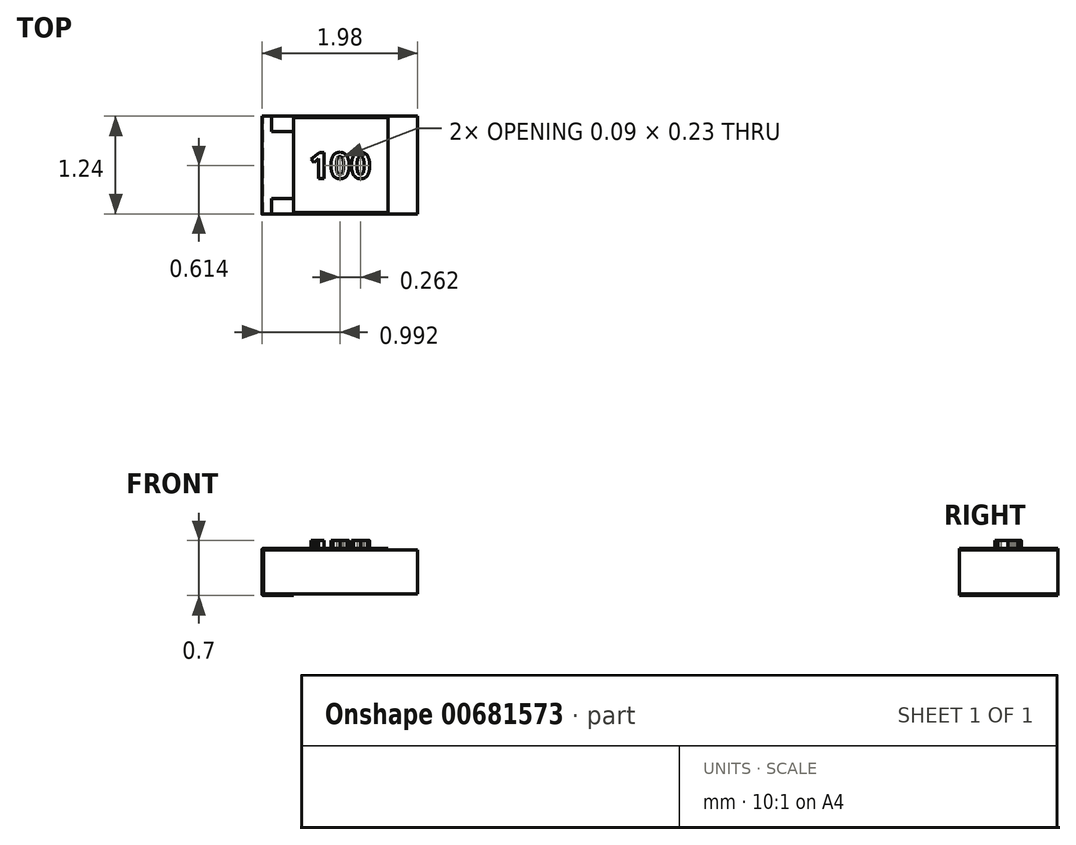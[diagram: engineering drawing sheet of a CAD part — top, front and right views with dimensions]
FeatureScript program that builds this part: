
annotation { "Feature Type Name" : "Feature", "Feature Type Description" : "" }
export const myFeature = defineFeature(function(context is Context, id is Id, definition is map)
    precondition{}
    {
        {
            assignVariable(context, id + "F0", {"name" : "size", "anyValue" : 3});
        }
        {
            assignVariable(context, id + "F1", {"name" : "width", "anyValue" : [.3, .5, .8, 1.25, 1.6, 2.5, 3.2, 2.5, 3.2][getVariable(context, 'size')]});
        }
        {
            assignVariable(context, id + "F2", {"name" : "r", "anyValue" : [0.02, 0.02, 0.02, 0.02, 0.02, 0.02, 0.02, 0.02, 0.02][getVariable(context, 'size')]});
        }
        {
            var Q0;
            Q0=qCreatedBy(makeId("Front.planeOp"),FACE);
            var sketch = newSketch(context, id + "F3", { "sketchPlane" : qUnion([Q0])});
            skLineSegment(sketch, "E0", {"start": v(-0.6, 0.6) * mm, "end": v(-0.98, 0.6) * mm});
            skLineSegment(sketch, "E1", {"start": v(-1, 0.58) * mm, "end": v(-1, 0.02) * mm});
            skLineSegment(sketch, "E2", {"start": v(-0.98, 0) * mm, "end": v(-0.6, 0) * mm});
            skLineSegment(sketch, "E3", {"start": v(-0.6, 0) * mm, "end": v(-0.6, 0.02) * mm});
            skLineSegment(sketch, "E4", {"start": v(-0.6, 0.02) * mm, "end": v(-0.98, 0.02) * mm});
            skLineSegment(sketch, "E5", {"start": v(-0.98, 0.02) * mm, "end": v(-0.98, 0.58) * mm});
            skLineSegment(sketch, "E6", {"start": v(-0.98, 0.58) * mm, "end": v(-0.6, 0.58) * mm});
            skLineSegment(sketch, "E7", {"start": v(-0.6, 0.58) * mm, "end": v(-0.6, 0.6) * mm});
            skLineSegment(sketch, "E8", {"start": v(-1, 0.3) * mm, "end": v(-0.98, 0.3) * mm, "construction": true});
            skPoint(sketch, "E9.visualSharp", {"position": v(-1, 0.6) * mm});
            skArc(sketch, "E9.filletArc", {"start": v(-0.98, 0.6) * mm, "mid": v(-1, 0.6) * mm, "end": v(-1, 0.58) * mm});
            skPoint(sketch, "E10.visualSharp", {"position": v(-1, 0) * mm});
            skArc(sketch, "E10.filletArc", {"start": v(-1, 0.02) * mm, "mid": v(-1, 0) * mm, "end": v(-0.98, 0) * mm});
            skArc(sketch, "E11.MirrorCS", {"start": v(1, 0.02) * mm, "mid": v(1, 0) * mm, "end": v(0.98, 0) * mm});
            skArc(sketch, "E12.MirrorCS", {"start": v(0.98, 0.6) * mm, "mid": v(1, 0.6) * mm, "end": v(1, 0.58) * mm});
            skLineSegment(sketch, "E13.MirrorCS", {"start": v(0.6, 0) * mm, "end": v(0.6, 0.02) * mm});
            skLineSegment(sketch, "E14.MirrorCS", {"start": v(0.6, 0.58) * mm, "end": v(0.6, 0.6) * mm});
            skLineSegment(sketch, "E15.MirrorCS", {"start": v(1, 0.3) * mm, "end": v(0.98, 0.3) * mm, "construction": true});
            skLineSegment(sketch, "E16.MirrorCS", {"start": v(1, 0.58) * mm, "end": v(1, 0.02) * mm});
            skLineSegment(sketch, "E17.MirrorCS", {"start": v(0.98, 0) * mm, "end": v(0.6, 0) * mm});
            skPoint(sketch, "E18.MirrorP", {"position": v(1, 0) * mm});
            skPoint(sketch, "E19.MirrorP", {"position": v(1, 0.6) * mm});
            skLineSegment(sketch, "E20.MirrorCS", {"start": v(0.6, 0.6) * mm, "end": v(0.98, 0.6) * mm});
            skLineSegment(sketch, "E21.MirrorCS", {"start": v(0.6, 0.02) * mm, "end": v(0.98, 0.02) * mm});
            skLineSegment(sketch, "E22.MirrorCS", {"start": v(0.98, 0.58) * mm, "end": v(0.6, 0.58) * mm});
            skLineSegment(sketch, "E23.MirrorCS", {"start": v(0.98, 0.02) * mm, "end": v(0.98, 0.58) * mm});
            skLineSegment(sketch, "E24", {"start": v(0.6, 0.58) * mm, "end": v(0.98, 0.58) * mm});
            skLineSegment(sketch, "E25", {"start": v(0.98, 0.02) * mm, "end": v(-0.98, 0.02) * mm});
            skLineSegment(sketch, "E26.bottom", {"start": v(-0.98, 0.58) * mm, "end": v(0.98, 0.58) * mm});
            skLineSegment(sketch, "E26.top", {"start": v(-0.98, 0.02) * mm, "end": v(0.98, 0.02) * mm});
            skLineSegment(sketch, "E26.left", {"start": v(-0.98, 0.58) * mm, "end": v(-0.98, 0.02) * mm});
            skLineSegment(sketch, "E26.right", {"start": v(0.98, 0.58) * mm, "end": v(0.98, 0.02) * mm});
            skLineSegment(sketch, "E27.bottom", {"start": v(-0.6, 0.6) * mm, "end": v(0.6, 0.6) * mm});
            skLineSegment(sketch, "E27.top", {"start": v(-0.6, 0.6) * mm, "end": v(0.6, 0.6) * mm});
            skLineSegment(sketch, "E27.left", {"start": v(-0.6, 0.6) * mm, "end": v(-0.6, 0.6) * mm});
            skLineSegment(sketch, "E27.right", {"start": v(0.6, 0.6) * mm, "end": v(0.6, 0.6) * mm});
            skLineSegment(sketch, "E28.bottom", {"start": v(0.6, 0.58) * mm, "end": v(-0.6, 0.58) * mm});
            skLineSegment(sketch, "E28.top", {"start": v(0.6, 0.58) * mm, "end": v(-0.6, 0.58) * mm});
            skLineSegment(sketch, "E28.left", {"start": v(0.6, 0.58) * mm, "end": v(0.6, 0.58) * mm});
            skLineSegment(sketch, "E28.right", {"start": v(-0.6, 0.58) * mm, "end": v(-0.6, 0.58) * mm});
            skSolve(sketch);
        }
        {
            var Q0;
            Q0=makeQuery(id+"F3.imprint","IMPRINT",FACE,{"disambiguationData":[TD([[makeQuery(id+"F3.imprint","IMPRINT",EDGE,{"derivedFrom":sQuery(id+"F3.wireOp",EDGE,"E0")}),1.0]])]});
            var Q1;
            Q1=makeQuery(id+"F3.imprint","IMPRINT",FACE,{"disambiguationData":[TD([[makeQuery(id+"F3.imprint","IMPRINT",EDGE,{"derivedFrom":sQuery(id+"F3.wireOp",EDGE,"E11.MirrorCS")}),-1.0]])]});
            extrude(context, id + "F4", {"entities" : qUnion([Q0, Q1]), "endBound" : BoundingType.SYMMETRIC, "depth" : (getVariable(context, 'width')) * mm, "offsetDistance" : 25 * mm});
        }
        {
            var Q0;
            Q0=makeQuery(id+"F3.imprint","IMPRINT",FACE,{"disambiguationData":[TD([[makeQuery(id+"F3.imprint","IMPRINT",EDGE,{"derivedFrom":sQuery(id+"F3.wireOp",EDGE,"E4")}),-1.0]])]});
            extrude(context, id + "F5", {"entities" : qUnion([Q0]), "endBound" : BoundingType.SYMMETRIC, "depth" : (getVariable(context, 'width')) * mm, "offsetDistance" : 25 * mm});
        }
        {
            var Q0;
            Q0=makeQuery(id+"F3.imprint","IMPRINT",FACE,{"disambiguationData":[TD([[makeQuery(id+"F3.imprint","IMPRINT",EDGE,{"derivedFrom":sQuery(id+"F3.wireOp",EDGE,"E7")}),-1.0]])]});
            extrude(context, id + "F6", {"entities" : qUnion([Q0]), "endBound" : BoundingType.SYMMETRIC, "depth" : ((getVariable(context, 'width')) - 2 * getVariable(context, 'r')) * mm, "offsetDistance" : 25 * mm});
        }
        {
            var Q0;
            Q0=makeQuery(id+"F6.opExtrude","SWEPT_FACE",FACE,{"disambiguationData":[OSD([sQuery(id+"F3.wireOp",EDGE,"E27.bottom")])]});
            var sketch = newSketch(context, id + "F7", { "sketchPlane" : qUnion([Q0])});
            skText(sketch, "E29", { "text": "100", "fontName": "OpenSans-Bold.ttf"});
            skPoint(sketch, "E30", {"position": v(0, 0) * mm});
            const initialGuessF7  = {"E29": [-0.0004, -0.00017, 1, 0, 0.00033]};
            skSetInitialGuess(sketch, initialGuessF7);
            skSolve(sketch);
        }
        {
            var Q0;
            Q0=makeQuery(id+"F7.imprint","IMPRINT",FACE,{"disambiguationData":[TD([[makeQuery(id+"F7.imprint","IMPRINT",EDGE,{"derivedFrom":sQuery(id+"F7.wireOp",EDGE,"E29.sketch_text.stroke-0")}),-1.0]])]});
            var Q1;
            Q1=makeQuery(id+"F7.imprint","IMPRINT",FACE,{"disambiguationData":[TD([[makeQuery(id+"F7.imprint","IMPRINT",EDGE,{"derivedFrom":sQuery(id+"F7.wireOp",EDGE,"E29.sketch_text.stroke-10")}),-1.0]])]});
            var Q2;
            Q2=makeQuery(id+"F7.imprint","IMPRINT",FACE,{"disambiguationData":[TD([[makeQuery(id+"F7.imprint","IMPRINT",EDGE,{"derivedFrom":sQuery(id+"F7.wireOp",EDGE,"E29.sketch_text.stroke-26")}),-1.0]])]});
            extrude(context, id + "F8", {"entities" : qUnion([Q0, Q1, Q2]), "depth" : .1 * mm, "offsetDistance" : 25 * mm});
        }
        {
            var Q0;
            Q0=makeQuery(id+"F4.opExtrude","SWEPT_FACE",FACE,{"disambiguationData":[OSD([sQuery(id+"F3.wireOp",EDGE,"E0")])]});
            var sketch = newSketch(context, id + "F9", { "sketchPlane" : qUnion([Q0])});
            skLineSegment(sketch, "E31.bottom", {"start": v(-0.6, -0.62) * mm, "end": v(-0.88, -0.62) * mm});
            skLineSegment(sketch, "E31.top", {"start": v(-0.6, -0.42) * mm, "end": v(-0.88, -0.42) * mm});
            skLineSegment(sketch, "E31.left", {"start": v(-0.6, -0.62) * mm, "end": v(-0.6, -0.42) * mm});
            skLineSegment(sketch, "E31.right", {"start": v(-0.88, -0.62) * mm, "end": v(-0.88, -0.42) * mm});
            skLineSegment(sketch, "E32.MirrorCS", {"start": v(-0.6, 0.42) * mm, "end": v(-0.88, 0.42) * mm});
            skLineSegment(sketch, "E33.MirrorCS", {"start": v(-0.6, 0.62) * mm, "end": v(-0.6, 0.42) * mm});
            skLineSegment(sketch, "E34.MirrorCS", {"start": v(-0.88, 0.62) * mm, "end": v(-0.88, 0.42) * mm});
            skLineSegment(sketch, "E35.MirrorCS", {"start": v(-0.6, 0.62) * mm, "end": v(-0.88, 0.62) * mm});
            skLineSegment(sketch, "E36.MirrorCS", {"start": v(0.6, 0.62) * mm, "end": v(0.88, 0.62) * mm});
            skLineSegment(sketch, "E37.MirrorCS", {"start": v(0.6, 0.62) * mm, "end": v(0.6, 0.42) * mm});
            skLineSegment(sketch, "E38.MirrorCS", {"start": v(0.88, 0.62) * mm, "end": v(0.88, 0.42) * mm});
            skLineSegment(sketch, "E39.MirrorCS", {"start": v(0.6, 0.42) * mm, "end": v(0.88, 0.42) * mm});
            skLineSegment(sketch, "E40.MirrorCS", {"start": v(0.6, -0.62) * mm, "end": v(0.6, -0.42) * mm});
            skLineSegment(sketch, "E41.MirrorCS", {"start": v(0.88, -0.62) * mm, "end": v(0.88, -0.42) * mm});
            skLineSegment(sketch, "E42.MirrorCS", {"start": v(0.6, -0.62) * mm, "end": v(0.88, -0.62) * mm});
            skLineSegment(sketch, "E43.MirrorCS", {"start": v(0.6, -0.42) * mm, "end": v(0.88, -0.42) * mm});
            skSolve(sketch);
        }
        {
            var Q0;
            Q0=makeQuery(id+"F9.imprint","IMPRINT",FACE,{"disambiguationData":[TD([[makeQuery(id+"F9.imprint","IMPRINT",EDGE,{"derivedFrom":sQuery(id+"F9.wireOp",EDGE,"E32.MirrorCS")}),-1.0]])]});
            var Q1;
            Q1=makeQuery(id+"F9.imprint","IMPRINT",FACE,{"disambiguationData":[TD([[makeQuery(id+"F9.imprint","IMPRINT",EDGE,{"derivedFrom":sQuery(id+"F9.wireOp",EDGE,"E31.bottom")}),-1.0]])]});
            extrude(context, id + "F10", {"entities" : qUnion([Q0, Q1]), "operationType" : NewBodyOperationType.REMOVE, "endBound" : BoundingType.UP_TO_NEXT, "oppositeDirection" : true, "depth" : 25 * mm, "offsetDistance" : 25 * mm});
        }
        {
            var Q0;
            Q0=makeQuery(id+"F9.imprint","IMPRINT",FACE,{"disambiguationData":[TD([[makeQuery(id+"F9.imprint","IMPRINT",EDGE,{"derivedFrom":sQuery(id+"F9.wireOp",EDGE,"E40.MirrorCS")}),-1.0]])]});
            var Q1;
            Q1=makeQuery(id+"F9.imprint","IMPRINT",FACE,{"disambiguationData":[TD([[makeQuery(id+"F9.imprint","IMPRINT",EDGE,{"derivedFrom":sQuery(id+"F9.wireOp",EDGE,"E36.MirrorCS")}),-1.0]])]});
            extrude(context, id + "F11", {"entities" : qUnion([Q0, Q1]), "operationType" : NewBodyOperationType.REMOVE, "endBound" : BoundingType.UP_TO_NEXT, "oppositeDirection" : true, "depth" : 25 * mm, "offsetDistance" : 25 * mm});
        }
    });
